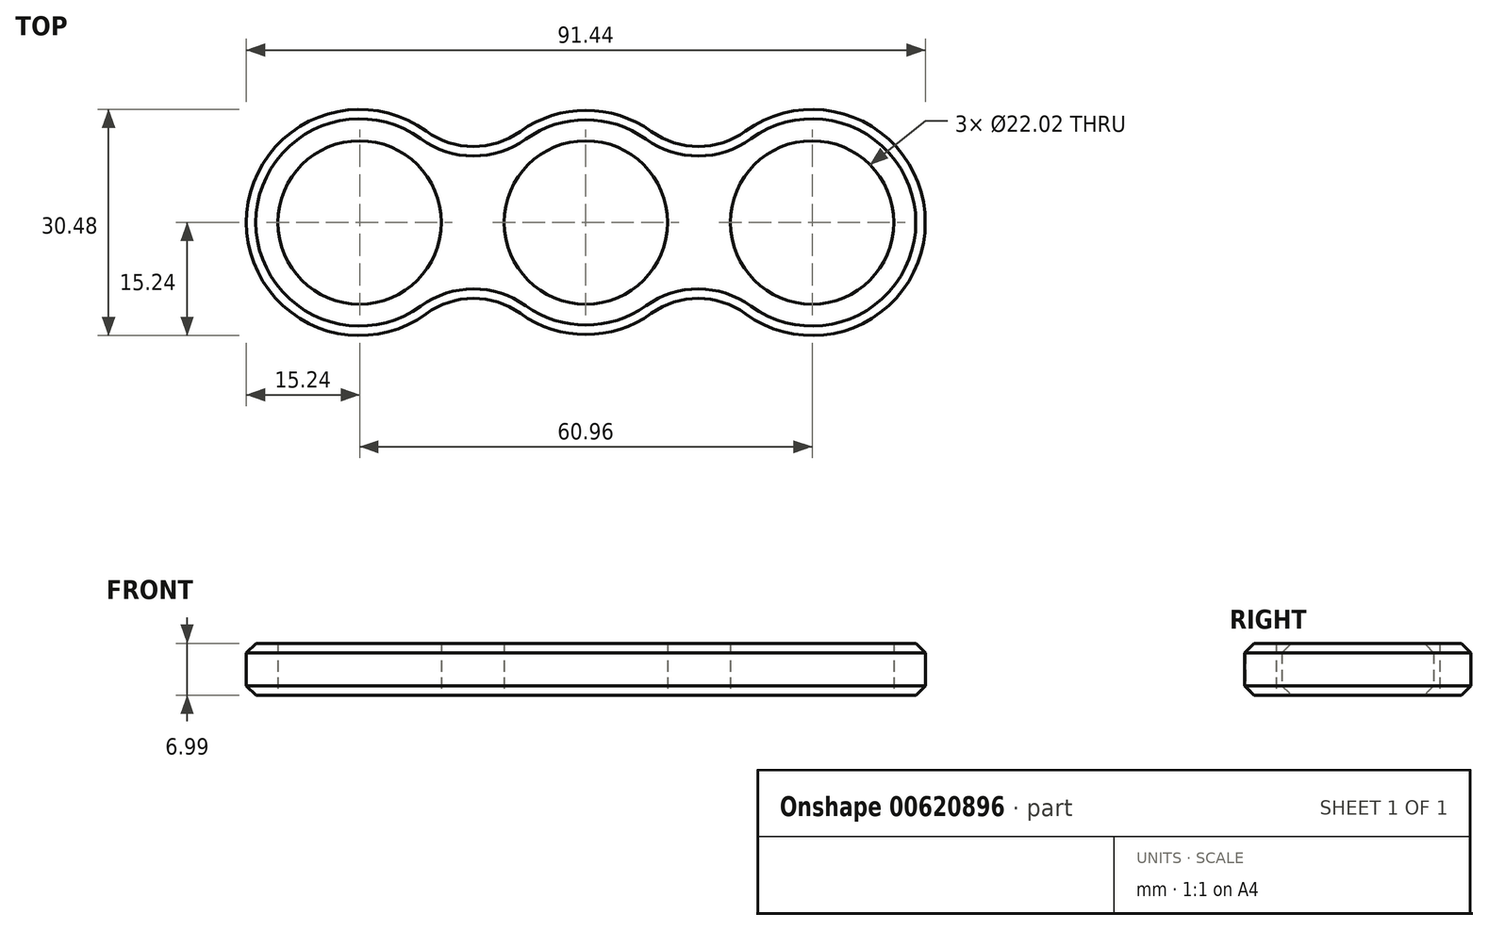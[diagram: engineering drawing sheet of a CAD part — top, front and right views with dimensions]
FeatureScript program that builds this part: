
annotation { "Feature Type Name" : "Feature", "Feature Type Description" : "" }
export const myFeature = defineFeature(function(context is Context, id is Id, definition is map)
    precondition{}
    {
        {
            var Q0;
            Q0=qCreatedBy(makeId("Top.planeOp"),FACE);
            var sketch = newSketch(context, id + "F0", { "sketchPlane" : qUnion([Q0])});
            skCircle(sketch, "E0", {"center": v(0, 0) * mm, "radius": 11.01 * mm});
            skLineSegment(sketch, "E1", {"start": v(0, 0) * mm, "end": v(30.48, 0) * mm});
            skLineSegment(sketch, "E2", {"start": v(0, 0) * mm, "end": v(-30.48, 0) * mm});
            skCircle(sketch, "E3", {"center": v(30.48, 0) * mm, "radius": 11.01 * mm});
            skCircle(sketch, "E4", {"center": v(-30.48, 0) * mm, "radius": 11.01 * mm});
            skCircle(sketch, "E5.cCircle", {"center": v(30.48, 0) * mm, "radius": 11.01 * mm, "construction": true});
            skPoint(sketch, "E5.0.midPoint", {"position": v(30.48, -11.01) * mm});
            skCircle(sketch, "E6", {"center": v(-30.48, 0) * mm, "radius": 15.24 * mm});
            skCircle(sketch, "E7", {"center": v(0, 0) * mm, "radius": 15.11 * mm});
            skCircle(sketch, "E8", {"center": v(30.48, 0) * mm, "radius": 15.24 * mm});
            skArc(sketch, "E9", {"start": v(21.5, -12.3) * mm, "mid": v(15.17, -10.23) * mm, "end": v(8.83, -12.27) * mm});
            skArc(sketch, "E10", {"start": v(8.83, 12.27) * mm, "mid": v(15.17, 10.23) * mm, "end": v(21.5, 12.3) * mm});
            skArc(sketch, "E11", {"start": v(-8.83, -12.27) * mm, "mid": v(-15.17, -10.23) * mm, "end": v(-21.5, -12.3) * mm});
            skArc(sketch, "E12", {"start": v(-21.5, 12.3) * mm, "mid": v(-15.17, 10.23) * mm, "end": v(-8.83, 12.27) * mm});
            skSolve(sketch);
        }
        {
            var Q0;
            Q0 = qSketchRegion(id + "F0", true);
            extrude(context, id + "F1", {"entities" : qUnion([Q0]), "depth" : 7 * mm, "offsetDistance" : 25.4 * mm});
        }
        {
            var Q0;
            Q0=makeQuery(id+"F1.opExtrude","CAP_EDGE",EDGE,{"disambiguationData":[OSD([sQuery(id+"F0.wireOp",EDGE,"E6")])],"isStart":false});
            chamfer(context, id + "F2", {"entities" : qUnion([Q0]), "width" : 1.27 * mm, "tangentPropagation" : true});
        }
        {
            var Q0;
            Q0=makeQuery(id+"F1.opExtrude","CAP_EDGE",EDGE,{"disambiguationData":[OSD([sQuery(id+"F0.wireOp",EDGE,"E6")])],"isStart":true});
            var Q1;
            Q1=makeQuery(id+"F1.opExtrude","CAP_EDGE",EDGE,{"disambiguationData":[OSD([sQuery(id+"F0.wireOp",EDGE,"E8")])],"isStart":true});
            var Q2;
            {var subQ0=sQuery(id+"F0.wireOp",EDGE,"E7");Q2=makeQuery(id+"F1.opExtrude","CAP_EDGE",EDGE,{"disambiguationData":[OSD([subQ0]),TDD([makeQuery(id+"F0.imprint","IMPRINT",EDGE,{"disambiguationData":[TD([[makeQuery(id+"F0.imprint","INTERSECT",VERTEX,{"derivedFrom":[subQ0,sQuery(id+"F0.wireOp",EDGE,"E9")]}),1.0]])],"derivedFrom":subQ0})])],"isStart":true});}
            var Q3;
            Q3=makeQuery(id+"F1.opExtrude","CAP_EDGE",EDGE,{"disambiguationData":[OSD([sQuery(id+"F0.wireOp",EDGE,"E9")])],"isStart":true});
            var Q4;
            Q4=makeQuery(id+"F1.opExtrude","CAP_EDGE",EDGE,{"disambiguationData":[OSD([sQuery(id+"F0.wireOp",EDGE,"E11")])],"isStart":true});
            var Q5;
            Q5=makeQuery(id+"F1.opExtrude","CAP_EDGE",EDGE,{"disambiguationData":[OSD([sQuery(id+"F0.wireOp",EDGE,"E12")])],"isStart":true});
            var Q6;
            {var subQ0=sQuery(id+"F0.wireOp",EDGE,"E7");Q6=makeQuery(id+"F1.opExtrude","CAP_EDGE",EDGE,{"disambiguationData":[OSD([subQ0]),TDD([makeQuery(id+"F0.imprint","IMPRINT",EDGE,{"disambiguationData":[TD([[makeQuery(id+"F0.imprint","INTERSECT",VERTEX,{"derivedFrom":[subQ0,sQuery(id+"F0.wireOp",EDGE,"E10")]}),-1.0]])],"derivedFrom":subQ0})])],"isStart":true});}
            var Q7;
            Q7=makeQuery(id+"F1.opExtrude","CAP_EDGE",EDGE,{"disambiguationData":[OSD([sQuery(id+"F0.wireOp",EDGE,"E10")])],"isStart":true});
            chamfer(context, id + "F3", {"entities" : qUnion([Q0, Q1, Q2, Q3, Q4, Q5, Q6, Q7]), "width" : 1.27 * mm, "tangentPropagation" : true});
        }
    });
